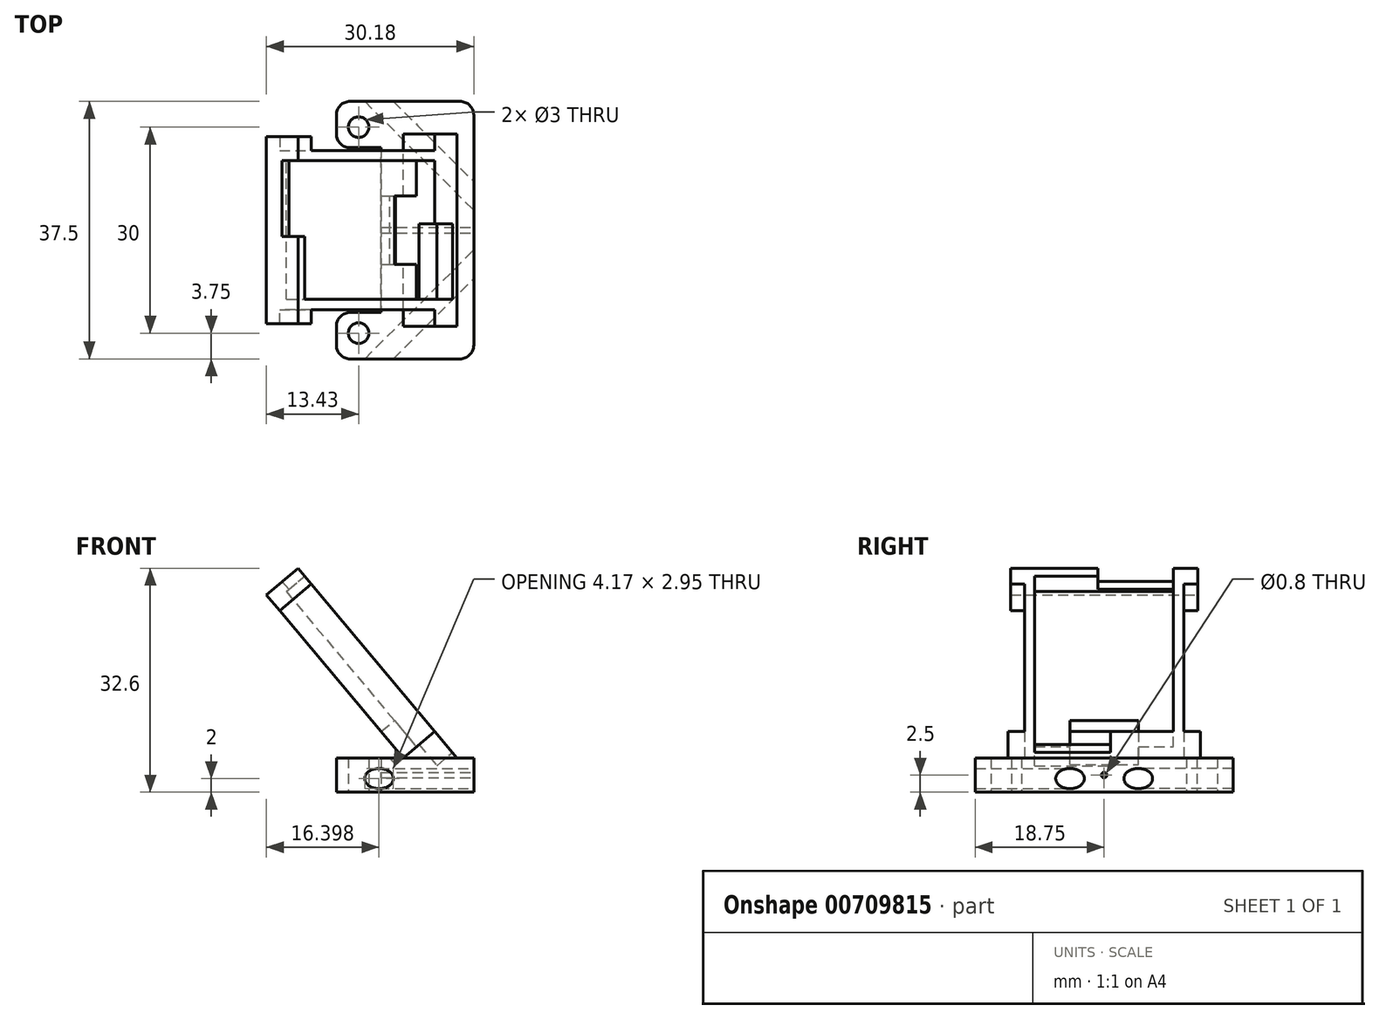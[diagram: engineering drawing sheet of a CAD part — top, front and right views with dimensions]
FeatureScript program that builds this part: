
annotation { "Feature Type Name" : "Feature", "Feature Type Description" : "" }
export const myFeature = defineFeature(function(context is Context, id is Id, definition is map)
    precondition{}
    {
        {
            var Q0;
            Q0=qCreatedBy(makeId("Top.planeOp"),FACE);
            var sketch = newSketch(context, id + "F0", { "sketchPlane" : qUnion([Q0])});
            skLineSegment(sketch, "E0.bottom", {"start": v(-10, -18.75) * mm, "end": v(10, -18.75) * mm});
            skLineSegment(sketch, "E0.top", {"start": v(-10, 18.75) * mm, "end": v(10, 18.75) * mm});
            skLineSegment(sketch, "E0.left", {"start": v(-10, -18.75) * mm, "end": v(-10, 18.75) * mm});
            skLineSegment(sketch, "E0.right", {"start": v(10, -18.75) * mm, "end": v(10, 18.75) * mm});
            skPoint(sketch, "E0.middle", {"position": v(0, 0) * mm});
            skSolve(sketch);
        }
        {
            var Q0;
            Q0=qSketchRegion(id+"F0",true);
            extrude(context, id + "F1", {"entities" : qUnion([Q0]), "depth" : 5 * mm, "offsetDistance" : 25 * mm});
        }
        {
            var Q0;
            Q0=qCreatedBy(makeId("Top.planeOp"),FACE);
            var sketch = newSketch(context, id + "F2", { "sketchPlane" : qUnion([Q0])});
            skLineSegment(sketch, "E1.bottom", {"start": v(-6.75, -15) * mm, "end": v(6.75, -15) * mm});
            skLineSegment(sketch, "E1.top", {"start": v(-6.75, 15) * mm, "end": v(6.75, 15) * mm});
            skLineSegment(sketch, "E1.left", {"start": v(-6.75, -15) * mm, "end": v(-6.75, 15) * mm});
            skLineSegment(sketch, "E1.right", {"start": v(6.75, -15) * mm, "end": v(6.75, 15) * mm});
            skPoint(sketch, "E1.middle", {"position": v(0, 0) * mm});
            skCircle(sketch, "E2", {"center": v(-6.75, -15) * mm, "radius": 1.5 * mm});
            skCircle(sketch, "E3", {"center": v(-6.75, 15) * mm, "radius": 1.5 * mm});
            skSolve(sketch);
        }
        {
            var Q0;
            Q0=sQuery(id+"F2.wireOp",VERTEX,"E1.left.start");
            var Q1;
            Q1=sQuery(id+"F2.wireOp",VERTEX,"E1.left.end");
            var Q2;
            Q2=makeQuery(id+"F1.opExtrude","SWEPT_BODY",BODY,{"disambiguationData":[OSD([sQuery(id+"F0.wireOp",EDGE,"E0.bottom"),sQuery(id+"F0.wireOp",EDGE,"E0.top"),sQuery(id+"F0.wireOp",EDGE,"E0.left"),sQuery(id+"F0.wireOp",EDGE,"E0.right")])]});
            hole(context, id + "F3", {"style" : HoleStyle.SIMPLE, "endStyle" : HoleEndStyle.THROUGH, "oppositeDirection" : true, "holeDiameter" : 3 * mm, "isTappedThrough" : true, "tappedDepth" : 12 * mm, "tapClearance" : 3, "locations" : qUnion([Q0, Q1]), "scope" : qUnion([Q2])});
        }
        {
            var Q0;
            Q0=qCreatedBy(makeId("Top.planeOp"),FACE);
            var sketch = newSketch(context, id + "F4", { "sketchPlane" : qUnion([Q0])});
            skLineSegment(sketch, "E4.bottom", {"start": v(-10, 12) * mm, "end": v(-3.5, 12) * mm});
            skLineSegment(sketch, "E4.top", {"start": v(-10, -12) * mm, "end": v(-3.5, -12) * mm});
            skLineSegment(sketch, "E4.left", {"start": v(-10, 12) * mm, "end": v(-10, -12) * mm});
            skLineSegment(sketch, "E4.right", {"start": v(-3.5, 12) * mm, "end": v(-3.5, -12) * mm});
            skSolve(sketch);
        }
        {
            var Q0;
            Q0=qSketchRegion(id+"F4",true);
            extrude(context, id + "F5", {"entities" : qUnion([Q0]), "operationType" : NewBodyOperationType.REMOVE, "depth" : 6 * mm, "offsetDistance" : 25 * mm});
        }
        {
            var Q0;
            Q0=makeQuery(id+"F1.opExtrude","SWEPT_EDGE",EDGE,{"disambiguationData":[OSD([sQuery(id+"F0.wireOp",EDGE,"E0.bottom"),sQuery(id+"F0.wireOp",EDGE,"E0.left")])]});
            var Q1;
            Q1=makeQuery(id+"F1.opExtrude","SWEPT_EDGE",EDGE,{"disambiguationData":[OSD([sQuery(id+"F0.wireOp",EDGE,"E0.bottom"),sQuery(id+"F0.wireOp",EDGE,"E0.right")])]});
            var Q2;
            Q2=makeQuery(id+"F1.opExtrude","SWEPT_EDGE",EDGE,{"disambiguationData":[OSD([sQuery(id+"F0.wireOp",EDGE,"E0.top"),sQuery(id+"F0.wireOp",EDGE,"E0.right")])]});
            var Q3;
            Q3=makeQuery(id+"F1.opExtrude","SWEPT_EDGE",EDGE,{"disambiguationData":[OSD([sQuery(id+"F0.wireOp",EDGE,"E0.top"),sQuery(id+"F0.wireOp",EDGE,"E0.left")])]});
            var Q4;
            Q4=makeQuery(id+"F5.boolean.opBoolean","COPY",EDGE,{"derivedFrom":makeQuery(id+"F5.opExtrude","SWEPT_EDGE",EDGE,{"disambiguationData":[OSD([sQuery(id+"F4.wireOp",EDGE,"E4.top"),sQuery(id+"F4.wireOp",EDGE,"E4.left")])]})});
            var Q5;
            Q5=makeQuery(id+"F5.boolean.opBoolean","COPY",EDGE,{"derivedFrom":makeQuery(id+"F5.opExtrude","SWEPT_EDGE",EDGE,{"disambiguationData":[OSD([sQuery(id+"F4.wireOp",EDGE,"E4.bottom"),sQuery(id+"F4.wireOp",EDGE,"E4.left")])]})});
            fillet(context, id + "F6", {"entities" : qUnion([Q0, Q1, Q2, Q3, Q4, Q5]), "radius" : 2 * mm, "tangentPropagation" : true, "allowEdgeOverflow" : false});
        }
        {
            var Q0;
            Q0=qCreatedBy(makeId("Top.planeOp"),FACE);
            var sketch = newSketch(context, id + "F7", { "sketchPlane" : qUnion([Q0])});
            skLineSegment(sketch, "E5", {"start": v(-10.17, 25.14) * mm, "end": v(14.97, 0) * mm});
            skLineSegment(sketch, "E6", {"start": v(-10.98, -25.95) * mm, "end": v(14.97, 0) * mm});
            skLineSegment(sketch, "E7", {"start": v(15.36, 5.25) * mm, "end": v(8.13, -1.98) * mm});
            skSolve(sketch);
        }
        {
            var Q0;
            Q0=sQuery(id+"F7.wireOp",EDGE,"E7");
            var Q1;
            Q1=qCreatedBy(makeId("Top.planeOp"),FACE);
            cPlane(context, id + "F8", {"entities" : qUnion([Q0, Q1]), "cplaneType" : CPlaneType.LINE_ANGLE, "offset" : 25 * mm, "angle" : 90 * degree, "width" : 150 * mm, "height" : 150 * mm});
        }
        {
            var Q0;
            Q0=qCreatedBy(id+"F8.planeOp",FACE);
            var sketch = newSketch(context, id + "F9", { "sketchPlane" : qUnion([Q0])});
            skLineSegment(sketch, "E8", {"start": v(10.58, 0) * mm, "end": v(10.58, 2) * mm});
            skCircle(sketch, "E9", {"center": v(10.58, 2) * mm, "radius": 1.48 * mm});
            skSolve(sketch);
        }
        {
            var Q0;
            Q0 = qSketchRegion(id + "F9", true);
            var Q1;
            Q1 = qSketchRegion(id + "F12", true);
            extrude(context, id + "F10", {"entities" : qUnion([Q0, Q1]), "operationType" : NewBodyOperationType.REMOVE, "oppositeDirection" : true, "depth" : 50 * mm, "offsetDistance" : 25 * mm});
        }
        {
            var Q0;
            Q0=makeQuery(id+"F1.opExtrude","SWEPT_BODY",BODY,{"disambiguationData":[OSD([sQuery(id+"F0.wireOp",EDGE,"E0.bottom"),sQuery(id+"F0.wireOp",EDGE,"E0.top"),sQuery(id+"F0.wireOp",EDGE,"E0.left"),sQuery(id+"F0.wireOp",EDGE,"E0.right")])]});
            var Q1;
            Q1=qCreatedBy(makeId("Front.planeOp"),FACE);
            mirror(context, id + "F11", {"operationType" : NewBodyOperationType.INTERSECT, "entities" : qUnion([Q0]), "mirrorPlane" : qUnion([Q1])});
        }
        {
            var Q0;
            Q0=makeQuery(id+"F1.opExtrude","CAP_FACE",FACE,{"disambiguationData":[OSD([sQuery(id+"F0.wireOp",EDGE,"E0.bottom"),sQuery(id+"F0.wireOp",EDGE,"E0.top"),sQuery(id+"F0.wireOp",EDGE,"E0.left"),sQuery(id+"F0.wireOp",EDGE,"E0.right")])],"isStart":false});
            var sketch = newSketch(context, id + "F12", { "sketchPlane" : qUnion([Q0])});
            skLineSegment(sketch, "E10", {"start": v(-0.25, 131.87) * mm, "end": v(-0.25, -129.82) * mm});
            skSolve(sketch);
        }
        {
            var Q0;
            Q0=sQuery(id+"F12.wireOp",EDGE,"E10");
            cPlane(context, id + "F13", {"entities" : qUnion([Q0]), "cplaneType" : CPlaneType.LINE_ANGLE, "offset" : 25 * mm, "angle" : 130 * degree, "width" : 150 * mm, "height" : 150 * mm});
        }
        {
            var Q0;
            Q0=qCreatedBy(id+"F13.planeOp",FACE);
            var sketch = newSketch(context, id + "F14", { "sketchPlane" : qUnion([Q0])});
            skLineSegment(sketch, "E11.bottom", {"start": v(-11.6, 35) * mm, "end": v(11.6, 35) * mm});
            skLineSegment(sketch, "E11.top", {"start": v(-11.6, 4) * mm, "end": v(11.6, 4) * mm});
            skLineSegment(sketch, "E11.left", {"start": v(-11.6, 35) * mm, "end": v(-11.6, 4) * mm});
            skLineSegment(sketch, "E11.right", {"start": v(11.6, 35) * mm, "end": v(11.6, 4) * mm});
            skSolve(sketch);
        }
        {
            var Q0;
            Q0 = qSketchRegion(id + "F14", true);
            extrude(context, id + "F15", {"entities" : qUnion([Q0]), "operationType" : NewBodyOperationType.ADD, "depth" : 6 * mm, "offsetDistance" : 25 * mm});
        }
        {
            var Q0;
            Q0=makeQuery(id+"F15.opExtrude","CAP_FACE",FACE,{"disambiguationData":[OSD([sQuery(id+"F14.wireOp",EDGE,"E11.bottom"),sQuery(id+"F14.wireOp",EDGE,"E11.top"),sQuery(id+"F14.wireOp",EDGE,"E11.left"),sQuery(id+"F14.wireOp",EDGE,"E11.right")])],"isStart":false});
            var sketch = newSketch(context, id + "F16", { "sketchPlane" : qUnion([Q0])});
            skLineSegment(sketch, "E12.bottom", {"start": v(-10.1, 33.5) * mm, "end": v(10.1, 33.5) * mm});
            skLineSegment(sketch, "E12.top", {"start": v(-10.1, 3.3) * mm, "end": v(10.1, 3.3) * mm});
            skLineSegment(sketch, "E12.left", {"start": v(-10.1, 33.5) * mm, "end": v(-10.1, 3.3) * mm});
            skLineSegment(sketch, "E12.right", {"start": v(10.1, 33.5) * mm, "end": v(10.1, 3.3) * mm});
            skSolve(sketch);
        }
        {
            var Q0;
            Q0 = qSketchRegion(id + "F16", true);
            extrude(context, id + "F17", {"entities" : qUnion([Q0]), "operationType" : NewBodyOperationType.REMOVE, "oppositeDirection" : true, "depth" : 3.5 * mm, "offsetDistance" : 25 * mm});
        }
        {
            var Q0;
            Q0=qCreatedBy(makeId("Front.planeOp"),FACE);
            var sketch = newSketch(context, id + "F18", { "sketchPlane" : qUnion([Q0])});
            skLineSegment(sketch, "E13", {"start": v(-0.25, 5) * mm, "end": v(7.58, 5) * mm});
            skLineSegment(sketch, "E14", {"start": v(7.58, 5) * mm, "end": v(4.35, 8.86) * mm});
            skLineSegment(sketch, "E15", {"start": v(4.35, 8.86) * mm, "end": v(-0.25, 5) * mm});
            skSolve(sketch);
        }
        {
            var Q0;
            Q0 = qSketchRegion(id + "F18", true);
            extrude(context, id + "F19", {"entities" : qUnion([Q0]), "operationType" : NewBodyOperationType.ADD, "endBound" : BoundingType.SYMMETRIC, "depth" : 28 * mm, "offsetDistance" : 25 * mm});
        }
        {
            var Q0;
            Q0=makeQuery(id+"F17.boolean.opBoolean","COPY",FACE,{"derivedFrom":makeQuery(id+"F17.opExtrude","CAP_FACE",FACE,{"disambiguationData":[OSD([sQuery(id+"F16.wireOp",EDGE,"E12.bottom"),sQuery(id+"F16.wireOp",EDGE,"E12.top"),sQuery(id+"F16.wireOp",EDGE,"E12.left"),sQuery(id+"F16.wireOp",EDGE,"E12.right")])],"isStart":false})});
            var sketch = newSketch(context, id + "F20", { "sketchPlane" : qUnion([Q0])});
            skLineSegment(sketch, "E16.bottom", {"start": v(-5, 9) * mm, "end": v(5, 9) * mm});
            skLineSegment(sketch, "E16.top", {"start": v(-5, 4) * mm, "end": v(5, 4) * mm});
            skLineSegment(sketch, "E16.left", {"start": v(-5, 9) * mm, "end": v(-5, 4) * mm});
            skLineSegment(sketch, "E16.right", {"start": v(5, 9) * mm, "end": v(5, 4) * mm});
            skSolve(sketch);
        }
        {
            var Q0;
            Q0 = qSketchRegion(id + "F20", true);
            extrude(context, id + "F21", {"entities" : qUnion([Q0]), "operationType" : NewBodyOperationType.REMOVE, "oppositeDirection" : true, "depth" : 4 * mm, "offsetDistance" : 25 * mm});
        }
        {
            var Q0;
            Q0=makeQuery(id+"F19.boolean.opBoolean","MERGE",FACE,{"derivedFrom":[makeQuery(id+"F15.opExtrude","CAP_FACE",FACE,{"disambiguationData":[OSD([sQuery(id+"F14.wireOp",EDGE,"E11.bottom"),sQuery(id+"F14.wireOp",EDGE,"E11.top"),sQuery(id+"F14.wireOp",EDGE,"E11.left"),sQuery(id+"F14.wireOp",EDGE,"E11.right")])],"isStart":false}),makeQuery(id+"F19.opExtrude","SWEPT_FACE",FACE,{"disambiguationData":[OSD([sQuery(id+"F18.wireOp",EDGE,"E14")])]})]});
            var sketch = newSketch(context, id + "F22", { "sketchPlane" : qUnion([Q0])});
            skLineSegment(sketch, "E17.bottom", {"start": v(-0.9, 35.5) * mm, "end": v(10.1, 35.5) * mm});
            skLineSegment(sketch, "E17.top", {"start": v(-0.9, 33.5) * mm, "end": v(10.1, 33.5) * mm});
            skLineSegment(sketch, "E17.left", {"start": v(-0.9, 35.5) * mm, "end": v(-0.9, 33.5) * mm});
            skLineSegment(sketch, "E17.right", {"start": v(10.1, 35.5) * mm, "end": v(10.1, 33.5) * mm});
            skSolve(sketch);
        }
        {
            var Q0;
            Q0 = qSketchRegion(id + "F22", true);
            extrude(context, id + "F23", {"entities" : qUnion([Q0]), "operationType" : NewBodyOperationType.REMOVE, "oppositeDirection" : true, "depth" : 3 * mm, "offsetDistance" : 25 * mm});
        }
        {
            var Q0;
            Q0=makeQuery(id+"F19.boolean.opBoolean","MERGE",FACE,{"derivedFrom":[makeQuery(id+"F15.opExtrude","CAP_FACE",FACE,{"disambiguationData":[OSD([sQuery(id+"F14.wireOp",EDGE,"E11.bottom"),sQuery(id+"F14.wireOp",EDGE,"E11.top"),sQuery(id+"F14.wireOp",EDGE,"E11.left"),sQuery(id+"F14.wireOp",EDGE,"E11.right")])],"isStart":false}),makeQuery(id+"F19.opExtrude","SWEPT_FACE",FACE,{"disambiguationData":[OSD([sQuery(id+"F18.wireOp",EDGE,"E14")])]})]});
            var sketch = newSketch(context, id + "F24", { "sketchPlane" : qUnion([Q0])});
            skLineSegment(sketch, "E18.bottom", {"start": v(-10.1, 4) * mm, "end": v(0.9, 4) * mm});
            skLineSegment(sketch, "E18.top", {"start": v(-10.1, 0) * mm, "end": v(0.9, 0) * mm});
            skLineSegment(sketch, "E18.left", {"start": v(-10.1, 4) * mm, "end": v(-10.1, 0) * mm});
            skLineSegment(sketch, "E18.right", {"start": v(0.9, 4) * mm, "end": v(0.9, 0) * mm});
            skSolve(sketch);
        }
        {
            var Q0;
            Q0 = qSketchRegion(id + "F24", true);
            extrude(context, id + "F25", {"entities" : qUnion([Q0]), "operationType" : NewBodyOperationType.REMOVE, "oppositeDirection" : true, "depth" : 3 * mm, "offsetDistance" : 25 * mm});
        }
        {
            var Q0;
            Q0=makeQuery(id+"F15.opExtrude","SWEPT_FACE",FACE,{"disambiguationData":[OSD([sQuery(id+"F14.wireOp",EDGE,"E11.left")])]});
            var sketch = newSketch(context, id + "F26", { "sketchPlane" : qUnion([Q0])});
            skLineSegment(sketch, "E19", {"start": v(-20.18, 28.75) * mm, "end": v(-15.58, 32.6) * mm});
            skLineSegment(sketch, "E20", {"start": v(-15.58, 32.6) * mm, "end": v(-13.65, 30.3) * mm});
            skLineSegment(sketch, "E21", {"start": v(-13.65, 30.3) * mm, "end": v(-18.25, 26.45) * mm});
            skLineSegment(sketch, "E22", {"start": v(-18.25, 26.45) * mm, "end": v(-20.18, 28.75) * mm});
            skSolve(sketch);
        }
        {
            var Q0;
            Q0 = qSketchRegion(id + "F26", true);
            extrude(context, id + "F27", {"entities" : qUnion([Q0]), "operationType" : NewBodyOperationType.ADD, "depth" : 2 * mm, "offsetDistance" : 25 * mm});
        }
        {
            var Q0;
            Q0=makeQuery(id+"F15.opExtrude","SWEPT_FACE",FACE,{"disambiguationData":[OSD([sQuery(id+"F14.wireOp",EDGE,"E11.right")])]});
            var sketch = newSketch(context, id + "F28", { "sketchPlane" : qUnion([Q0])});
            skLineSegment(sketch, "E23", {"start": v(15.58, 32.6) * mm, "end": v(20.18, 28.75) * mm});
            skLineSegment(sketch, "E24", {"start": v(20.18, 28.75) * mm, "end": v(18.25, 26.45) * mm});
            skLineSegment(sketch, "E25", {"start": v(18.25, 26.45) * mm, "end": v(13.65, 30.3) * mm});
            skLineSegment(sketch, "E26", {"start": v(13.65, 30.3) * mm, "end": v(15.58, 32.6) * mm});
            skSolve(sketch);
        }
        {
            var Q0;
            Q0 = qSketchRegion(id + "F28", true);
            extrude(context, id + "F29", {"entities" : qUnion([Q0]), "operationType" : NewBodyOperationType.ADD, "depth" : 2 * mm, "offsetDistance" : 25 * mm});
        }
        {
            var Q0;
            Q0=makeQuery(id+"F1.opExtrude","SWEPT_FACE",FACE,{"disambiguationData":[OSD([sQuery(id+"F0.wireOp",EDGE,"E0.right")])]});
            var sketch = newSketch(context, id + "F30", { "sketchPlane" : qUnion([Q0])});
            skCircle(sketch, "E27", {"center": v(0, 2.5) * mm, "radius": 0.4 * mm});
            skSolve(sketch);
        }
        {
            var Q0;
            Q0 = qSketchRegion(id + "F30", true);
            extrude(context, id + "F31", {"entities" : qUnion([Q0]), "operationType" : NewBodyOperationType.REMOVE, "oppositeDirection" : true, "depth" : 70 * mm, "offsetDistance" : 25 * mm});
        }
    });
